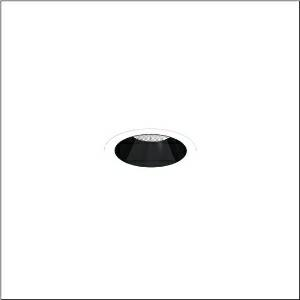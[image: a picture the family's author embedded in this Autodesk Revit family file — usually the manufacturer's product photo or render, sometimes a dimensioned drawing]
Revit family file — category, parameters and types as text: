
# Revit family: lunis_21_m_51db17mc91c
name_source: partatom
category: Lighting Fixtures
units: mm (PartAtom-declared; Revit-internal decimal feet)

## family parameters
Cut with Voids When Loaded = No
Host = Face
Light Source = No
Part Type = Normal
Room Calculation Point = No
Round Connector Dimension = Use Diameter
Shared = No

## types (1)
- --- (1 x LED, 3420 lm, 25.5 W, 6500K)
    Apparent Load = 26 VA
    CIE Flux Codes = 98 100 100 100 100
    Color Rendering = 80
    Color Temperature = 6500K
    Default Elevation = 1800 mm
    Description = Lunis 21,  M, downlight, light control with lens, of PMMA, anti glare with reflector, of PC, light emission: direct distribution, LED rated luminous flux: 1.570lm, light colour: 830/840/865, with terminal, 3-pole, mains connection: 220..240V, AC/DC, 0/50..60Hz, housing, round, of diecast aluminium, traffic white (RAL 9016), diameter: 115mm, clamping range: 1..40mm, protection rating (complete): IP20, protection rating (on room side): IP54, insulation class (complete): insulation class II (safety insulation), certification: CE, impact resistance: IK03, packaging unit: 1 piece
    Height = 0 mm  [stored 0 ft]
    Lamp = 1 x LED
    Lamp Light Flux = 3420 lm
    Lamp Power = 25.5 W
    Lamp count = 1
    Length = 115 mm
    Luminous efficacy = 134 lm/W
    Manufacturer = Siteco
    ModVariant = No
    Model = 51DB17MC91C
    Mounting Place = Ceiling
    Mounting Type = Recessed
    Number of Poles = 1
    OnlyDefault = Yes
    Power Factor = 1
    Product Name = Lunis 21 M
    Product group = downlight
    ProductGroupID = 400
    Protection Class = Protection class II
    Protection Degree = IP 20
    RLX_Detail_Level = 1
    RLX_Emergency_Light_Flux = 0 lm
    RLX_Emergency_Type = 0
    RLX_Emergency_Type_DB = No
    RlxData = <blob elided: 15041 chars, md5=d0d254fb>
    Socket = socket
    Standby Power = 0 W
    System Light Flux = 3420 lm
    System Power = 26 W
    Type Comments = individual setting: colour temperature 6500K, luminous flux: 100 % | (ON | ON | OFF | OFF) | 700 mA
    Type Image = l_1290854.jpg
    URL = http://relux.com
    VarID = @adj_020132
    Voltage = 0 V
    Weight = 0.00 kg
    Width = 0 mm  [stored 0 ft]

note: [stored X ft] marks values corroborated as IEEE doubles in the binary element streams (Revit-internal decimal feet)

## geometry (parser evidence)
native form markers: Sweep x12
no freeform markers — native parametric forms only
